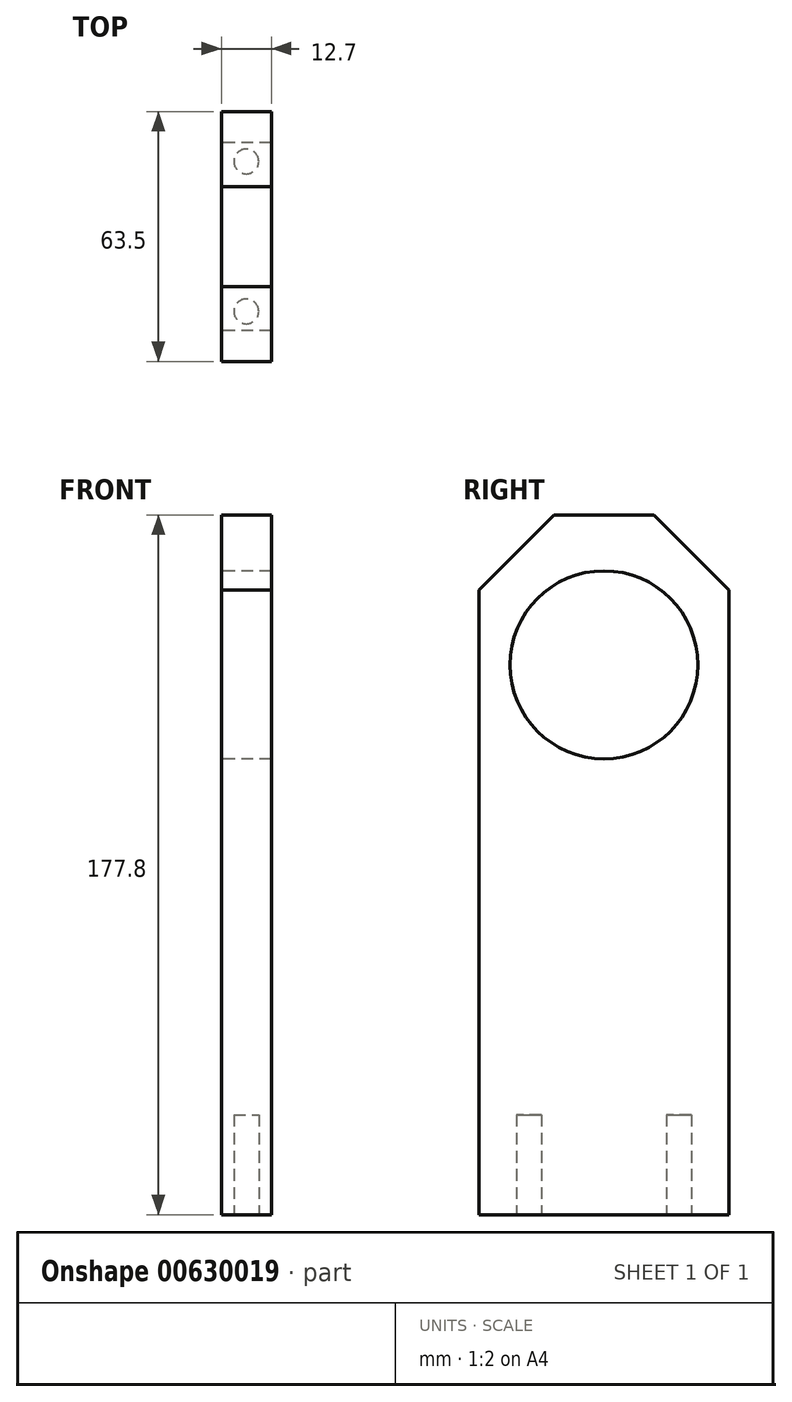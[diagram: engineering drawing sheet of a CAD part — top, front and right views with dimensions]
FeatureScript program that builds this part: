
annotation { "Feature Type Name" : "Feature", "Feature Type Description" : "" }
export const myFeature = defineFeature(function(context is Context, id is Id, definition is map)
    precondition{}
    {
        {
            var Q0;
            Q0=qCreatedBy(makeId("Right.planeOp"),FACE);
            var sketch = newSketch(context, id + "F0", { "sketchPlane" : qUnion([Q0])});
            skLineSegment(sketch, "E0", {"start": v(0, 88.9) * mm, "end": v(12.7, 88.9) * mm});
            skLineSegment(sketch, "E1", {"start": v(0, -88.9) * mm, "end": v(31.75, -88.9) * mm});
            skLineSegment(sketch, "E2", {"start": v(31.75, -88.9) * mm, "end": v(31.75, 69.85) * mm});
            skLineSegment(sketch, "E3", {"start": v(12.7, 88.9) * mm, "end": v(31.75, 69.85) * mm});
            skLineSegment(sketch, "E4.MirrorCS", {"start": v(0, 88.9) * mm, "end": v(-12.7, 88.9) * mm});
            skLineSegment(sketch, "E5.MirrorCS", {"start": v(0, -88.9) * mm, "end": v(-31.75, -88.9) * mm});
            skLineSegment(sketch, "E6.MirrorCS", {"start": v(-12.7, 88.9) * mm, "end": v(-31.75, 69.85) * mm});
            skLineSegment(sketch, "E7.MirrorCS", {"start": v(-31.75, -88.9) * mm, "end": v(-31.75, 69.85) * mm});
            skSolve(sketch);
        }
        {
            var Q0;
            Q0=makeQuery(id+"F0.imprint","IMPRINT",FACE,{"disambiguationData":[TD([[makeQuery(id+"F0.imprint","IMPRINT",EDGE,{"derivedFrom":sQuery(id+"F0.wireOp",EDGE,"E0")}),-1.0]])]});
            extrude(context, id + "F1", {"entities" : qUnion([Q0]), "depth" : 12.7 * mm, "offsetDistance" : 25.4 * mm});
        }
        {
            var Q0;
            Q0=qCreatedBy(makeId("Right.planeOp"),FACE);
            var sketch = newSketch(context, id + "F2", { "sketchPlane" : qUnion([Q0])});
            skCircle(sketch, "E8", {"center": v(0, 50.8) * mm, "radius": 23.88 * mm});
            skSolve(sketch);
        }
        {
            var Q0;
            Q0=makeQuery(id+"F2.imprint","IMPRINT",FACE,{"disambiguationData":[TD([[makeQuery(id+"F2.imprint","IMPRINT",EDGE,{"derivedFrom":sQuery(id+"F2.wireOp",EDGE,"E8")}),1.0]])]});
            extrude(context, id + "F3", {"entities" : qUnion([Q0]), "operationType" : NewBodyOperationType.REMOVE, "endBound" : BoundingType.THROUGH_ALL, "depth" : 25.4 * mm, "offsetDistance" : 25.4 * mm});
        }
        {
            var Q0;
            Q0=makeQuery(id+"F1.opExtrude","SWEPT_FACE",FACE,{"disambiguationData":[OSD([sQuery(id+"F0.wireOp",EDGE,"E1"),sQuery(id+"F0.wireOp",EDGE,"E5.MirrorCS")])]});
            var sketch = newSketch(context, id + "F4", { "sketchPlane" : qUnion([Q0])});
            skLineSegment(sketch, "E9", {"start": v(6.35, 31.75) * mm, "end": v(6.35, -31.75) * mm, "construction": true});
            skLineSegment(sketch, "E10", {"start": v(0, 19.05) * mm, "end": v(15.1, 19.05) * mm, "construction": true});
            skLineSegment(sketch, "E11", {"start": v(0, -19.05) * mm, "end": v(16.26, -19.05) * mm, "construction": true});
            skCircle(sketch, "E12", {"center": v(6.35, 19.05) * mm, "radius": 3.18 * mm});
            skCircle(sketch, "E13", {"center": v(6.35, -19.05) * mm, "radius": 3.18 * mm});
            skSolve(sketch);
        }
        {
            var Q0;
            Q0=makeQuery(id+"F4.imprint","IMPRINT",FACE,{"disambiguationData":[TD([[makeQuery(id+"F4.imprint","IMPRINT",EDGE,{"derivedFrom":sQuery(id+"F4.wireOp",EDGE,"E12")}),1.0]])]});
            var Q1;
            Q1=makeQuery(id+"F4.imprint","IMPRINT",FACE,{"disambiguationData":[TD([[makeQuery(id+"F4.imprint","IMPRINT",EDGE,{"derivedFrom":sQuery(id+"F4.wireOp",EDGE,"E13")}),1.0]])]});
            extrude(context, id + "F5", {"entities" : qUnion([Q0, Q1]), "operationType" : NewBodyOperationType.REMOVE, "oppositeDirection" : true, "depth" : 25.4 * mm, "offsetDistance" : 25.4 * mm});
        }
    });
